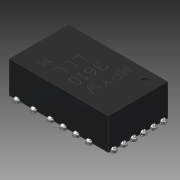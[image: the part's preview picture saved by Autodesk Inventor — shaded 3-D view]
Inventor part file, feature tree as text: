
AUTODESK INVENTOR PART (.ipt)
format: ipt  version: 2016 (Build 200138000, 138)  size: 598,528 bytes
history: native  units: mm
features: extrude x5, sketch x4, projected_geometry x2, plane x1, fillet x1
ambient origin geometry x8: Origin, YZ Plane, XZ Plane, XY Plane, X Axis, Y Axis, Z Axis, Center Point
bodies: Body1 (feature_tree)
feature tree (13):
  extrude  "Extrusion4"  Depth=5.0mm
  sketch  "Sketch11"  dims[d9=1.6mm d10=0.0mm d11=0.4mm]
  extrude  "Extrusion5"  Depth=0.4mm
  extrude  "Extrusion6"  Depth=3.65mm
  plane  "Work Plane1"
  extrude  "Extrusion7"  Depth=0.6mm
  extrude  "Extrusion8"  Depth=0.55mm
  fillet  "Fillet1"  Radius=0.01mm
  sketch  "Sketch10"  dims[d7=3.0mm d8=5.0mm]
  projected_geometry  "Projected Loop1"
  sketch  "Sketch12"  dims[d12=0.4mm d13=3.65mm]
  projected_geometry  "Projected Loop3"
  sketch  "Sketch13"  dims[d14=2.0mm d15=0.6mm d16=0.55mm d17=0.01mm d18=0.0mm d19=0.075mm d20=0.0mm d22=0.3mm d26=0.05mm d29=0.25mm d30=0.15mm d31=0.2mm d33=2.0mm d34=0.85mm d39=0.8mm d40=0.35mm d41=0.35mm d43=0.45mm d44=0.15mm d49=0.1mm d50=0.2mm d51=0.2mm d52=0.2mm d53=0.55mm d54=0.125mm d55=0.125mm d56=0.2mm d57=0.0mm d60=1.15mm d61=1.53mm d62=0.79mm d63=0.5mm d64=0.1mm d65=0.1mm d66=0.0mm d67=0.15mm]
